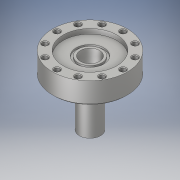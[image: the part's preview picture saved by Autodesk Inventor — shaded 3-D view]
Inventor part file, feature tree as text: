
AUTODESK INVENTOR PART (.ipt)
format: ipt  version: 2018 (Build 220112000, 112)  size: 211,968 bytes
history: native  units: in
note: dims shown in document units (in); Inventor stores cm internally (conversion verified against a paired STEP export)
features: sketch x6, extrude x5, chamfer x3, hole x1, pattern_circular x1
ambient origin geometry x8: Origin, YZ Plane, XZ Plane, XY Plane, X Axis, Y Axis, Z Axis, Center Point
bodies: Solid1 (feature_tree)
feature tree (16):
  extrude  "Extrusion1"  Depth=0.5in TaperAngle=0.0deg
  chamfer  "Chamfer1"  Distance=0.0291in Angle=45.0deg
  extrude  "Extrusion2"  Depth=0.113in TaperAngle=0.0deg
  extrude  "Extrusion3"  Depth=0.05in
  extrude  "Extrusion4"  Depth=0.5in
  chamfer  "Chamfer2"  Distance=0.04in
  extrude  "Extrusion5"  Depth=0.45in
  hole  "Hole1"  [1 undecoded]
  chamfer  "Chamfer3"  Angle=30.0deg  [1 undecoded]
  pattern_circular  "Circular Pattern1"  Angle=45.0deg  [1 undecoded]
  sketch  "Sketch1"  dims[d0=1.755in d1=0.5in d2=0.0in d3=0.0291in d4=0.125in d5=45.0deg]
  sketch  "Sketch2"  dims[d6=1.26in d7=0.113in d8=0.0in]
  sketch  "Sketch3"  dims[d9=0.658in d10=0.05in]
  sketch  "Sketch4"  dims[d11=0.04in d12=0.0in d13=0.5in d14=0.04in d15=0.0in]
  sketch  "Sketch5"  dims[d16=0.0291in d17=0.125in d18=45.0deg d19=0.45in]
  sketch  "Sketch6"  dims[d20=1.5in d21=0.0in d22=0.775in d23=30.0deg d24=0.125in d25=0.75in d26=0.375in d27=0.25in d28=0.5635in d29=1.0in d30=0.8108in d31=0.015in d32=0.125in d33=45.0deg d34=4.7244in d35=360.0deg]
note: 3 required parameter values undecoded (feature->parameter linkage not recoverable at this tier; creation-order binding heuristic only, values carry confidence <= 0.55)
